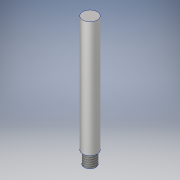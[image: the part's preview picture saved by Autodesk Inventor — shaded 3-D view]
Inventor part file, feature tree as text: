
AUTODESK INVENTOR PART (.ipt)
format: ipt  version: 2019 (Build 230136000, 136)  size: 101,888 bytes
history: native  units: mm
features: extrude x2, sketch x2, other x1
ambient origin geometry x8: Origin, YZ Plane, XZ Plane, XY Plane, X Axis, Y Axis, Z Axis, Center Point
bodies: Solide1 (feature_tree)
feature tree (5):
  extrude  "Extrusion1"  Depth=4.0mm
  extrude  "Extrusion2"  Depth=4.25mm TaperAngle=0.0deg
  other  "Filetage1"
  sketch  "Esquisse1"
  sketch  "Esquisse2"
